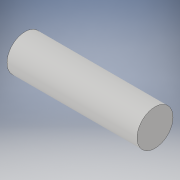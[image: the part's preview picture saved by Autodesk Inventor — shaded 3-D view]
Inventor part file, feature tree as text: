
AUTODESK INVENTOR PART (.ipt)
format: ipt  version: 2019 (Build 230136000, 136)  size: 89,088 bytes
history: native  units: mm
features: extrude x1, sketch x1
ambient origin geometry x8: Origin, YZ Plane, XZ Plane, XY Plane, X Axis, Y Axis, Z Axis, Center Point
bodies: Solid1 (feature_tree)
feature tree (2):
  extrude  "Extrusion1"  Depth=65.0mm TaperAngle=0.0deg
  sketch  "Sketch1"  dims[d0=18.0mm d1=65.0mm d2=0.0mm]
